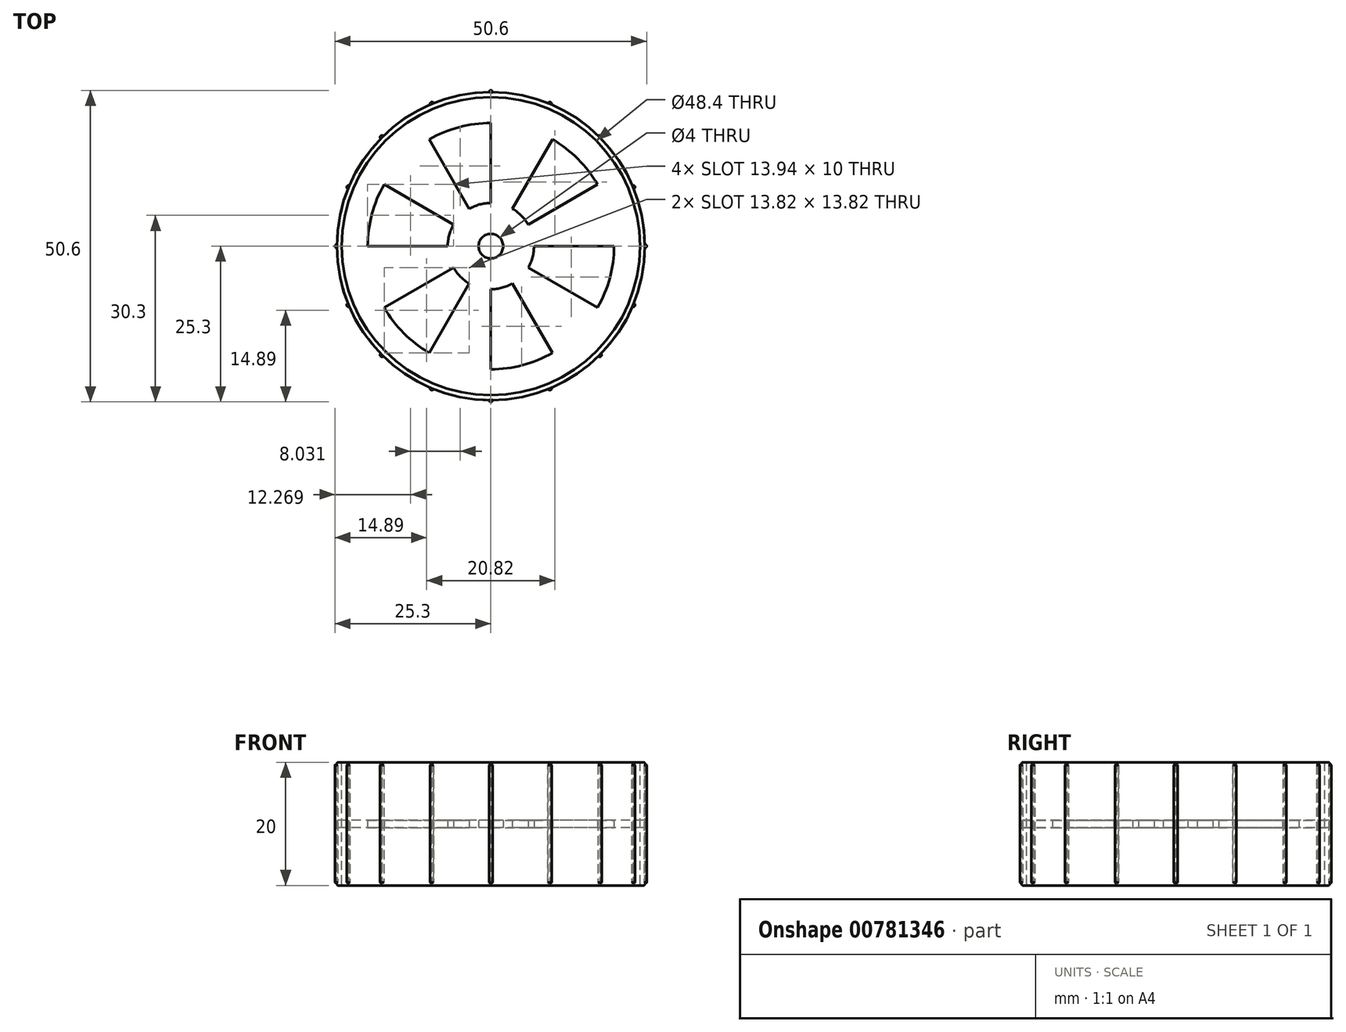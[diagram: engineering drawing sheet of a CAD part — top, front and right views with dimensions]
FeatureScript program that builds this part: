
annotation { "Feature Type Name" : "Feature", "Feature Type Description" : "" }
export const myFeature = defineFeature(function(context is Context, id is Id, definition is map)
    precondition{}
    {
        {
            var Q0;
            Q0=qCreatedBy(makeId("Front.planeOp"),FACE);
            var sketch = newSketch(context, id + "F0", { "sketchPlane" : qUnion([Q0])});
            skLineSegment(sketch, "E0", {"start": v(-25, 9.8) * mm, "end": v(-25, -9.8) * mm});
            skLineSegment(sketch, "E1", {"start": v(-24.8, -10) * mm, "end": v(-24.4, -10) * mm});
            skLineSegment(sketch, "E2", {"start": v(-24.2, -9.8) * mm, "end": v(-24.2, 9.8) * mm});
            skLineSegment(sketch, "E3", {"start": v(-24.4, 10) * mm, "end": v(-24.8, 10) * mm});
            skPoint(sketch, "E4.visualSharp", {"position": v(-25, 10) * mm});
            skArc(sketch, "E4.filletArc", {"start": v(-24.8, 10) * mm, "mid": v(-24.94, 9.94) * mm, "end": v(-25, 9.8) * mm});
            skPoint(sketch, "E5.visualSharp", {"position": v(-24.2, 10) * mm});
            skArc(sketch, "E5.filletArc", {"start": v(-24.2, 9.8) * mm, "mid": v(-24.26, 9.94) * mm, "end": v(-24.4, 10) * mm});
            skPoint(sketch, "E6.visualSharp", {"position": v(-24.2, -10) * mm});
            skArc(sketch, "E6.filletArc", {"start": v(-24.4, -10) * mm, "mid": v(-24.26, -9.94) * mm, "end": v(-24.2, -9.8) * mm});
            skPoint(sketch, "E7.visualSharp", {"position": v(-25, -10) * mm});
            skArc(sketch, "E7.filletArc", {"start": v(-25, -9.8) * mm, "mid": v(-24.94, -9.94) * mm, "end": v(-24.8, -10) * mm});
            skLineSegment(sketch, "E8", {"start": v(0, 25.1) * mm, "end": v(0, -30.52) * mm, "construction": true});
            skSolve(sketch);
        }
        {
            var Q0;
            Q0 = qSketchRegion(id + "F0", true);
            var Q1;
            Q1=sQuery(id+"F0.wireOp",EDGE,"E8");
            revolve(context, id + "F1", {"surfaceOperationType" : NewSurfaceOperationType.NEW, "entities" : qUnion([Q0]), "axis" : qUnion([Q1]), "revolveType" : RevolveType.FULL});
        }
        {
            var Q0;
            Q0=qCreatedBy(makeId("Front.planeOp"),FACE);
            var sketch = newSketch(context, id + "F2", { "sketchPlane" : qUnion([Q0])});
            skLineSegment(sketch, "E9.0", {"start": v(-25, 9.8) * mm, "end": v(-25, -9.8) * mm});
            skLineSegment(sketch, "E10", {"start": v(-25, 9.8) * mm, "end": v(-25.3, 9.54) * mm});
            skLineSegment(sketch, "E11", {"start": v(-25.3, 9.54) * mm, "end": v(-25.3, -9.54) * mm});
            skLineSegment(sketch, "E12", {"start": v(-25.3, -9.54) * mm, "end": v(-25, -9.8) * mm});
            skSolve(sketch);
        }
        {
            var Q0;
            Q0 = qSketchRegion(id + "F2", true);
            var Q1;
            Q1=sQuery(id+"F2.wireOp",EDGE,"E9.0");
            revolve(context, id + "F3", {"surfaceOperationType" : NewSurfaceOperationType.NEW, "entities" : qUnion([Q0]), "axis" : qUnion([Q1]), "revolveType" : RevolveType.TWO_DIRECTIONS, "angle" : 120 * degree, "angleBack" : 240 * degree});
        }
        {
            var Q0;
            Q0=makeQuery(id+"F3.opRevolve","SWEPT_BODY",BODY,{"disambiguationData":[OSD([sQuery(id+"F2.wireOp",EDGE,"E9.0"),sQuery(id+"F2.wireOp",EDGE,"E10"),sQuery(id+"F2.wireOp",EDGE,"E11"),sQuery(id+"F2.wireOp",EDGE,"E12")])]});
            var Q1;
            Q1=sQuery(id+"F0.wireOp",EDGE,"E8");
            circularPattern(context, id + "F4", {"entities" : qUnion([Q0]), "axis" : qUnion([Q1]), "angle" : 360 * degree, "instanceCount" : 16, "equalSpace" : true});
        }
        {
            var Q0;
            Q0=qCreatedBy(makeId("Top.planeOp"),FACE);
            var sketch = newSketch(context, id + "F5", { "sketchPlane" : qUnion([Q0])});
            skCircle(sketch, "E13", {"center": v(0, 0) * mm, "radius": 24.9 * mm});
            skSolve(sketch);
        }
        {
            var Q0;
            Q0 = qSketchRegion(id + "F5", true);
            extrude(context, id + "F6", {"entities" : qUnion([Q0]), "endBound" : BoundingType.SYMMETRIC, "depth" : 1.2 * mm, "offsetDistance" : 25 * mm});
        }
        {
            var Q0;
            Q0=qCreatedBy(makeId("Top.planeOp"),FACE);
            var sketch = newSketch(context, id + "F7", { "sketchPlane" : qUnion([Q0])});
            skCircle(sketch, "E14.0.0", {"center": v(0, 0) * mm, "radius": 24.9 * mm, "construction": true});
            skArc(sketch, "E15", {"start": v(10, 17.32) * mm, "mid": v(14.14, 14.14) * mm, "end": v(17.32, 10) * mm});
            skArc(sketch, "E16", {"start": v(3.5, 6.06) * mm, "mid": v(4.95, 4.95) * mm, "end": v(6.06, 3.5) * mm});
            skLineSegment(sketch, "E17", {"start": v(-2, -3.47) * mm, "end": v(9.75, 16.89) * mm, "construction": true});
            skLineSegment(sketch, "E18", {"start": v(-7.59, -4.38) * mm, "end": v(16.28, 9.4) * mm, "construction": true});
            skLineSegment(sketch, "E19", {"start": v(0, 0) * mm, "end": v(23.68, 0) * mm, "construction": true});
            skLineSegment(sketch, "E20", {"start": v(0, 0) * mm, "end": v(0, 15.72) * mm, "construction": true});
            skLineSegment(sketch, "E21", {"start": v(6.06, 3.5) * mm, "end": v(17.32, 10) * mm});
            skLineSegment(sketch, "E22", {"start": v(3.5, 6.06) * mm, "end": v(10, 17.32) * mm});
            skArc(sketch, "E23.1.0", {"start": v(-20, 0) * mm, "mid": v(-19.32, 5.18) * mm, "end": v(-17.32, 10) * mm});
            skArc(sketch, "E23.1.1", {"start": v(-7, 0) * mm, "mid": v(-6.76, 1.81) * mm, "end": v(-6.06, 3.5) * mm});
            skLineSegment(sketch, "E23.1.2", {"start": v(7.59, -4.38) * mm, "end": v(-16.28, 9.4) * mm, "construction": true});
            skArc(sketch, "E23.2.0", {"start": v(10, -17.32) * mm, "mid": v(5.18, -19.32) * mm, "end": v(0, -20) * mm});
            skArc(sketch, "E23.2.1", {"start": v(3.5, -6.06) * mm, "mid": v(1.81, -6.76) * mm, "end": v(0, -7) * mm});
            skLineSegment(sketch, "E23.2.2", {"start": v(0, 8.76) * mm, "end": v(0, -18.8) * mm, "construction": true});
            skArc(sketch, "E24.1.0", {"start": v(-10, 17.32) * mm, "mid": v(-5.18, 19.32) * mm, "end": v(0, 20) * mm});
            skArc(sketch, "E24.1.1", {"start": v(-3.5, 6.06) * mm, "mid": v(-1.81, 6.76) * mm, "end": v(0, 7) * mm});
            skLineSegment(sketch, "E24.1.2", {"start": v(-3.5, 6.06) * mm, "end": v(-10, 17.32) * mm});
            skLineSegment(sketch, "E24.1.3", {"start": v(0, 7) * mm, "end": v(0, 20) * mm});
            skLineSegment(sketch, "E24.2.2", {"start": v(-7, 0) * mm, "end": v(-20, 0) * mm});
            skLineSegment(sketch, "E24.2.3", {"start": v(-6.06, 3.5) * mm, "end": v(-17.32, 10) * mm});
            skArc(sketch, "E24.3.0", {"start": v(-10, -17.32) * mm, "mid": v(-14.14, -14.14) * mm, "end": v(-17.32, -10) * mm});
            skArc(sketch, "E24.3.1", {"start": v(-3.5, -6.06) * mm, "mid": v(-4.95, -4.95) * mm, "end": v(-6.06, -3.5) * mm});
            skLineSegment(sketch, "E24.3.2", {"start": v(-3.5, -6.06) * mm, "end": v(-10, -17.32) * mm});
            skLineSegment(sketch, "E24.3.3", {"start": v(-6.06, -3.5) * mm, "end": v(-17.32, -10) * mm});
            skLineSegment(sketch, "E24.4.2", {"start": v(3.5, -6.06) * mm, "end": v(10, -17.32) * mm});
            skLineSegment(sketch, "E24.4.3", {"start": v(0, -7) * mm, "end": v(0, -20) * mm});
            skArc(sketch, "E24.5.0", {"start": v(20, 0) * mm, "mid": v(19.32, -5.18) * mm, "end": v(17.32, -10) * mm});
            skArc(sketch, "E24.5.1", {"start": v(7, 0) * mm, "mid": v(6.76, -1.81) * mm, "end": v(6.06, -3.5) * mm});
            skLineSegment(sketch, "E24.5.2", {"start": v(7, 0) * mm, "end": v(20, 0) * mm});
            skLineSegment(sketch, "E24.5.3", {"start": v(6.06, -3.5) * mm, "end": v(17.32, -10) * mm});
            skCircle(sketch, "E25", {"center": v(0, 0) * mm, "radius": 2 * mm});
            skSolve(sketch);
        }
        {
            var Q0;
            Q0 = qSketchRegion(id + "F7", true);
            extrude(context, id + "F8", {"entities" : qUnion([Q0]), "operationType" : NewBodyOperationType.REMOVE, "endBound" : BoundingType.SYMMETRIC, "depth" : 25 * mm, "offsetDistance" : 25 * mm});
        }
    });
